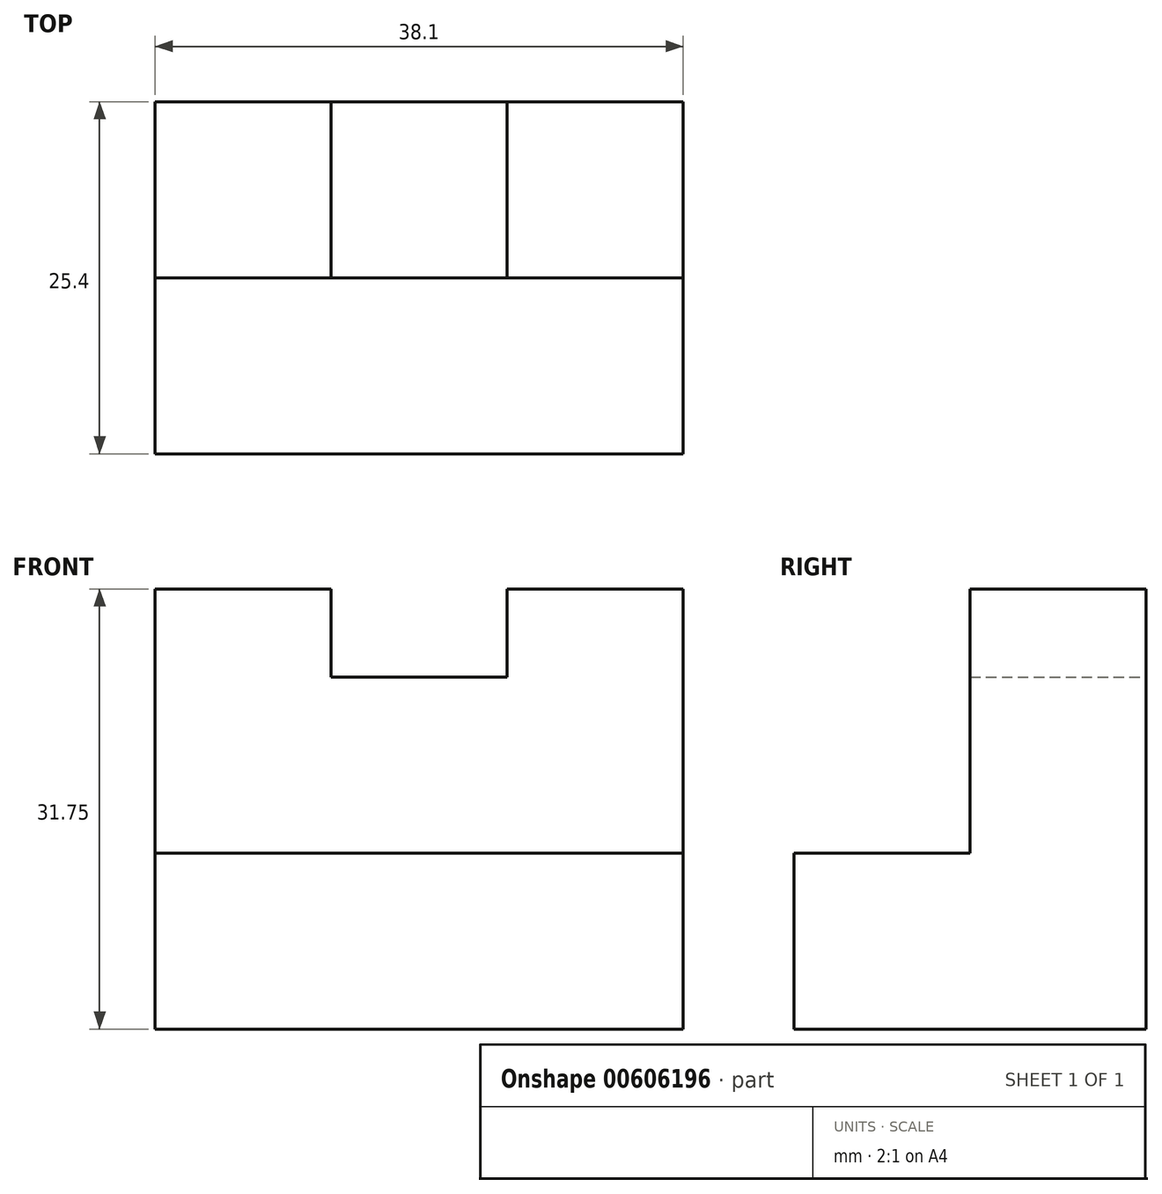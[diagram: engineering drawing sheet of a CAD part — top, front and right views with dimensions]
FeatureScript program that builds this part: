
annotation { "Feature Type Name" : "Feature", "Feature Type Description" : "" }
export const myFeature = defineFeature(function(context is Context, id is Id, definition is map)
    precondition{}
    {
        {
            var Q0;
            Q0=qCreatedBy(makeId("Right.planeOp"),FACE);
            var sketch = newSketch(context, id + "F0", { "sketchPlane" : qUnion([Q0])});
            skLineSegment(sketch, "E0", {"start": v(0, 0) * mm, "end": v(25.4, 0) * mm});
            skLineSegment(sketch, "E1", {"start": v(25.4, 0) * mm, "end": v(25.4, 31.75) * mm});
            skLineSegment(sketch, "E2", {"start": v(25.4, 31.75) * mm, "end": v(12.7, 31.75) * mm});
            skLineSegment(sketch, "E3", {"start": v(12.7, 31.75) * mm, "end": v(12.7, 12.7) * mm});
            skLineSegment(sketch, "E4", {"start": v(12.7, 12.7) * mm, "end": v(0, 12.7) * mm});
            skLineSegment(sketch, "E5", {"start": v(0, 12.7) * mm, "end": v(0, 0) * mm});
            skSolve(sketch);
        }
        {
            var Q0;
            Q0 = qSketchRegion(id + "F0", true);
            extrude(context, id + "F1", {"entities" : qUnion([Q0]), "depth" : 38.1 * mm, "offsetDistance" : 25.4 * mm});
        }
        {
            var Q0;
            Q0=makeQuery(id+"F1.opExtrude","SWEPT_FACE",FACE,{"disambiguationData":[OSD([sQuery(id+"F0.wireOp",EDGE,"E2")])]});
            var sketch = newSketch(context, id + "F2", { "sketchPlane" : qUnion([Q0])});
            skLineSegment(sketch, "E6", {"start": v(0, 12.7) * mm, "end": v(12.7, 12.7) * mm});
            skLineSegment(sketch, "E7", {"start": v(12.7, 12.7) * mm, "end": v(12.7, 25.4) * mm});
            skLineSegment(sketch, "E8", {"start": v(12.7, 25.4) * mm, "end": v(25.4, 25.4) * mm});
            skLineSegment(sketch, "E9", {"start": v(25.4, 25.4) * mm, "end": v(25.4, 12.7) * mm});
            skLineSegment(sketch, "E10", {"start": v(25.4, 12.7) * mm, "end": v(12.7, 12.7) * mm});
            skSolve(sketch);
        }
        {
            var Q0;
            Q0=makeQuery(id+"F2.imprint","IMPRINT",FACE,{"disambiguationData":[TD([[makeQuery(id+"F2.imprint","IMPRINT",EDGE,{"derivedFrom":sQuery(id+"F2.wireOp",EDGE,"E7")}),-1.0]])]});
            extrude(context, id + "F3", {"entities" : qUnion([Q0]), "operationType" : NewBodyOperationType.REMOVE, "oppositeDirection" : true, "depth" : 6.35 * mm, "offsetDistance" : 25.4 * mm});
        }
    });
